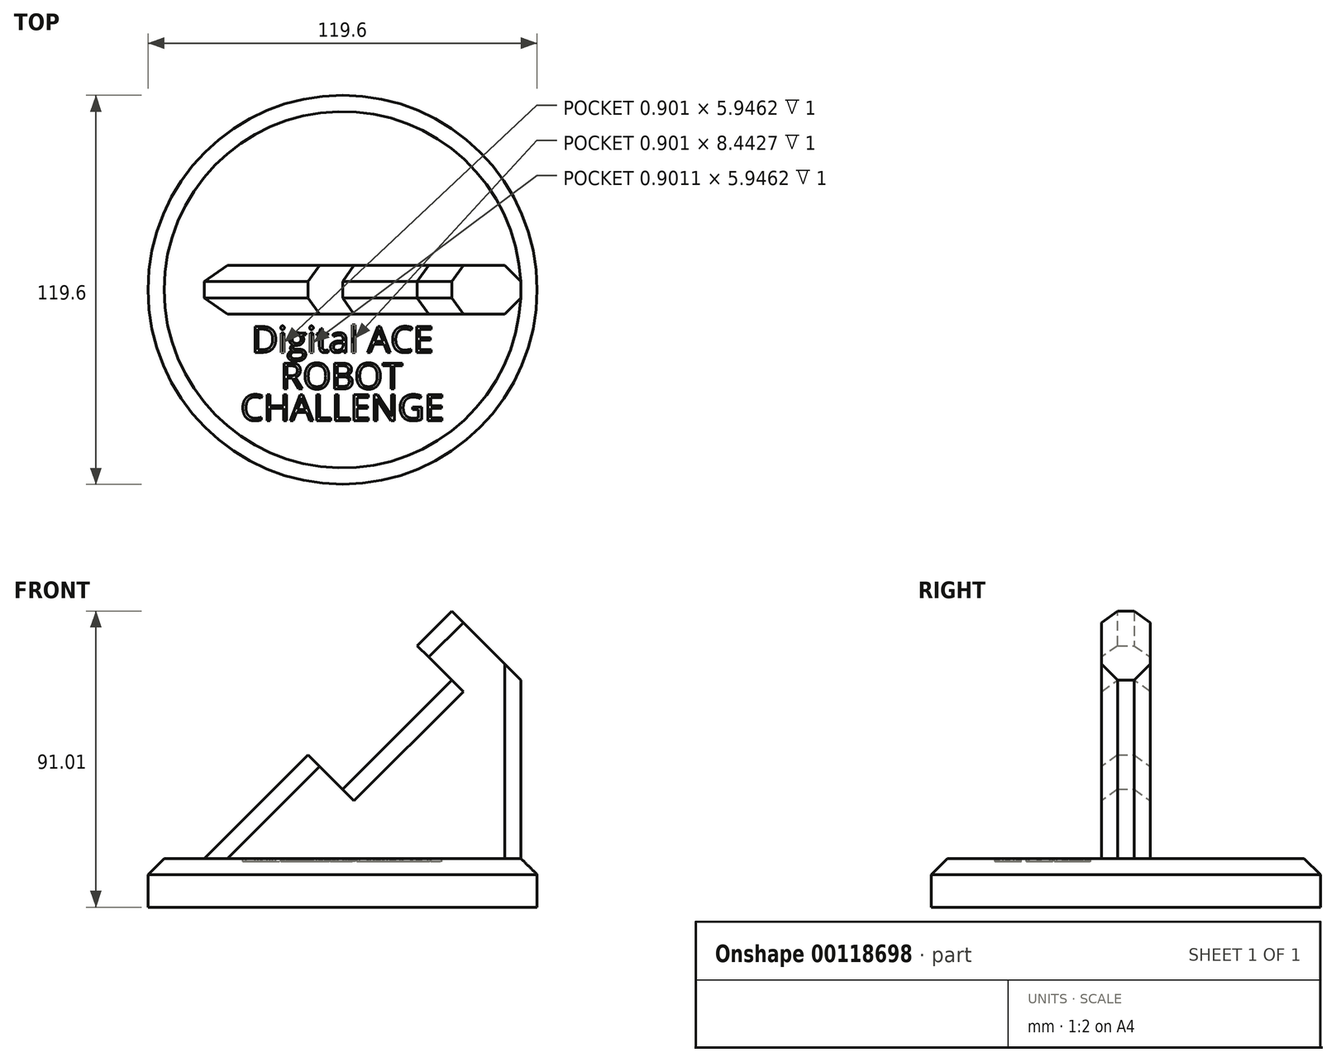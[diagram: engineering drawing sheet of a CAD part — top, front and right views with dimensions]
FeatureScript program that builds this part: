
annotation { "Feature Type Name" : "Feature", "Feature Type Description" : "" }
export const myFeature = defineFeature(function(context is Context, id is Id, definition is map)
    precondition{}
    {
        {
            var Q0;
            Q0=qCreatedBy(makeId("Front.planeOp"),FACE);
            var sketch = newSketch(context, id + "F0", { "sketchPlane" : qUnion([Q0])});
            skLineSegment(sketch, "E0", {"start": v(-80, 0) * mm, "end": v(0, 80) * mm, "construction": true});
            skLineSegment(sketch, "E1", {"start": v(-80, 0) * mm, "end": v(-46.41, 33.59) * mm});
            skLineSegment(sketch, "E2", {"start": v(-46.41, 33.59) * mm, "end": v(-57.02, 44.2) * mm});
            skLineSegment(sketch, "E3", {"start": v(-80, 0) * mm, "end": v(-90.6, 10.6) * mm});
            skLineSegment(sketch, "E4", {"start": v(-90.6, 10.6) * mm, "end": v(-101.21, 0) * mm});
            skLineSegment(sketch, "E5", {"start": v(-101.21, 0) * mm, "end": v(-80, -21.21) * mm});
            skLineSegment(sketch, "E6", {"start": v(-57.02, 44.2) * mm, "end": v(-46.41, 54.8) * mm});
            skLineSegment(sketch, "E7", {"start": v(-46.41, 54.8) * mm, "end": v(-25.2, 33.59) * mm});
            skLineSegment(sketch, "E8", {"start": v(-25.2, 33.59) * mm, "end": v(-25.2, -21.21) * mm});
            skLineSegment(sketch, "E9", {"start": v(-25.2, -21.21) * mm, "end": v(-80, -21.21) * mm, "construction": true});
            skLineSegment(sketch, "E10", {"start": v(-52.6, -21.21) * mm, "end": v(-52.6, 73.71) * mm, "construction": true});
            skLineSegment(sketch, "E11", {"start": v(-52.6, -21.21) * mm, "end": v(-52.6, -70.46) * mm, "construction": true});
            skLineSegment(sketch, "E12", {"start": v(-80, -21.21) * mm, "end": v(-80, -75.81) * mm, "construction": true});
            skLineSegment(sketch, "E13.MirrorCS", {"start": v(-134.8, -21.21) * mm, "end": v(-80, -21.21) * mm, "construction": true});
            skLineSegment(sketch, "E14", {"start": v(-80, -21.21) * mm, "end": v(-134.8, -21.21) * mm});
            skLineSegment(sketch, "E15", {"start": v(-134.8, -21.21) * mm, "end": v(-139.8, -21.21) * mm});
            skLineSegment(sketch, "E16", {"start": v(-139.8, -21.21) * mm, "end": v(-139.8, -36.21) * mm});
            skLineSegment(sketch, "E17", {"start": v(-139.8, -36.21) * mm, "end": v(-80, -36.21) * mm});
            skLineSegment(sketch, "E18", {"start": v(-80, -21.21) * mm, "end": v(-80, -36.21) * mm});
            skLineSegment(sketch, "E19", {"start": v(-80, -21.21) * mm, "end": v(-25.2, -21.21) * mm});
            skLineSegment(sketch, "E20.MirrorCS", {"start": v(-25.2, -21.21) * mm, "end": v(-20.2, -21.21) * mm, "construction": true});
            skLineSegment(sketch, "E21.MirrorCS", {"start": v(-20.2, -21.21) * mm, "end": v(-20.2, -36.21) * mm, "construction": true});
            skLineSegment(sketch, "E22.MirrorCS", {"start": v(-20.2, -36.21) * mm, "end": v(-80, -36.21) * mm, "construction": true});
            skSolve(sketch);
        }
        {
            var Q0;
            Q0=makeQuery(id+"F0.imprint","IMPRINT",FACE,{"disambiguationData":[TD([[makeQuery(id+"F0.imprint","IMPRINT",EDGE,{"derivedFrom":sQuery(id+"F0.wireOp",EDGE,"E1")}),-1.0]])]});
            extrude(context, id + "F1", {"entities" : qUnion([Q0]), "depth" : 15 * mm, "symmetric" : true});
        }
        {
            var Q0;
            Q0=makeQuery(id+"F0.imprint","IMPRINT",FACE,{"disambiguationData":[TD([[makeQuery(id+"F0.imprint","IMPRINT",EDGE,{"derivedFrom":sQuery(id+"F0.wireOp",EDGE,"E14")}),1.0]])]});
            var Q1;
            Q1=sQuery(id+"F0.wireOp",EDGE,"E18");
            revolve(context, id + "F2", {"operationType" : NewBodyOperationType.ADD, "entities" : qUnion([Q0]), "axis" : qUnion([Q1]), "revolveType" : RevolveType.FULL});
        }
        {
            var Q0;
            Q0=makeQuery(id+"F2.opRevolve","SWEPT_EDGE",EDGE,{"disambiguationData":[OSD([sQuery(id+"F0.wireOp",EDGE,"E15"),sQuery(id+"F0.wireOp",EDGE,"E16")])]});
            chamfer(context, id + "F3", {"entities" : qUnion([Q0]), "width" : 5 * mm, "tangentPropagation" : true});
        }
        {
            var Q0;
            Q0=makeQuery(id+"F1.opExtrude","CAP_EDGE",EDGE,{"disambiguationData":[OSD([sQuery(id+"F0.wireOp",EDGE,"E8")])],"isStart":false});
            var Q1;
            Q1=makeQuery(id+"F1.opExtrude","CAP_EDGE",EDGE,{"disambiguationData":[OSD([sQuery(id+"F0.wireOp",EDGE,"E8")])],"isStart":true});
            var Q2;
            Q2=makeQuery(id+"F1.opExtrude","CAP_EDGE",EDGE,{"disambiguationData":[OSD([sQuery(id+"F0.wireOp",EDGE,"E1")])],"isStart":false});
            var Q3;
            Q3=makeQuery(id+"F1.opExtrude","CAP_EDGE",EDGE,{"disambiguationData":[OSD([sQuery(id+"F0.wireOp",EDGE,"E1")])],"isStart":true});
            chamfer(context, id + "F4", {"entities" : qUnion([Q0, Q1, Q2, Q3]), "width" : 5 * mm, "tangentPropagation" : true});
        }
        {
            var Q0;
            Q0=makeQuery(id+"F1.opExtrude","SWEPT_FACE",FACE,{"disambiguationData":[OSD([sQuery(id+"F0.wireOp",EDGE,"E7")])]});
            var sketch = newSketch(context, id + "F5", { "sketchPlane" : qUnion([Q0])});
            skLineSegment(sketch, "E23", {"start": v(-71.57, -7.5) * mm, "end": v(-56.57, -7.5) * mm, "construction": true});
            skCircle(sketch, "E24", {"center": v(-64.07, 0) * mm, "radius": 4.25 * mm});
            skPoint(sketch, "E24.centerSnap0", {"position": v(-64.07, -7.5) * mm});
            skPoint(sketch, "E24.centerSnap1", {"position": v(-71.57, 0) * mm});
            skSolve(sketch);
        }
        {
            var Q0;
            Q0 = qSketchRegion(id + "F5", true);
            var Q1;
            Q1=makeQuery(id+"F1.opExtrude","SWEPT_FACE",FACE,{"disambiguationData":[OSD([sQuery(id+"F0.wireOp",EDGE,"E5")])]});
            extrude(context, id + "F6", {"entities" : qUnion([Q0]), "operationType" : NewBodyOperationType.REMOVE, "endBound" : BoundingType.UP_TO_SURFACE, "oppositeDirection" : true, "endBoundEntityFace" : qUnion([Q1]), "depth" : 25 * mm});
        }
        {
            var Q0;
            Q0=makeQuery(id+"F1.opExtrude","CAP_EDGE",EDGE,{"disambiguationData":[OSD([sQuery(id+"F0.wireOp",EDGE,"E6")])],"isStart":false});
            var Q1;
            Q1=makeQuery(id+"F1.opExtrude","CAP_EDGE",EDGE,{"disambiguationData":[OSD([sQuery(id+"F0.wireOp",EDGE,"E6")])],"isStart":true});
            var Q2;
            Q2=makeQuery(id+"F1.opExtrude","CAP_EDGE",EDGE,{"disambiguationData":[OSD([sQuery(id+"F0.wireOp",EDGE,"E4")])],"isStart":true});
            var Q3;
            Q3=makeQuery(id+"F1.opExtrude","CAP_EDGE",EDGE,{"disambiguationData":[OSD([sQuery(id+"F0.wireOp",EDGE,"E4")])],"isStart":false});
            chamfer(context, id + "F7", {"entities" : qUnion([Q0, Q1, Q2, Q3]), "width" : 5 * mm, "tangentPropagation" : true});
        }
        {
            var Q0;
            Q0=makeQuery(id+"F1.opExtrude","SWEPT_FACE",FACE,{"disambiguationData":[OSD([sQuery(id+"F0.wireOp",EDGE,"E5")])]});
            var Q1;
            Q1=makeQuery(id+"F2.opRevolve","SWEPT_FACE",FACE,{"disambiguationData":[OSD([sQuery(id+"F0.wireOp",EDGE,"E14"),sQuery(id+"F0.wireOp",EDGE,"E15")])]});
            extrude(context, id + "F8", {"entities" : qUnion([Q0]), "operationType" : NewBodyOperationType.ADD, "endBound" : BoundingType.UP_TO_SURFACE, "endBoundEntityFace" : qUnion([Q1]), "depth" : 25 * mm});
        }
        {
            var Q0;
            {var subQ0=sQuery(id+"F0.wireOp",EDGE,"E4");var subQ12=sQuery(id+"F0.wireOp",EDGE,"E15");Q0=makeQuery(id+"F8.boolean.opBoolean","SPLIT",FACE,{"disambiguationData":[TD([makeQuery(id+"F1.opExtrude","SWEPT_FACE",FACE,{"disambiguationData":[OSD([subQ0])]})])],"derivedFrom":makeQuery(id+"F2.opRevolve","SWEPT_FACE",FACE,{"disambiguationData":[OSD([sQuery(id+"F0.wireOp",EDGE,"E14"),subQ12])]})});}
            var sketch = newSketch(context, id + "F9", { "sketchPlane" : qUnion([Q0])});
            skText(sketch, "E25", { "text": "Digital ACE", "fontName": "OpenSans-Regular.ttf"});
            skText(sketch, "E26", { "text": "ROBOT", "fontName": "OpenSans-Regular.ttf"});
            skText(sketch, "E27", { "text": "CHALLENGE", "fontName": "OpenSans-Regular.ttf"});
            skLineSegment(sketch, "E28", {"start": v(-80, -22.5) * mm, "end": v(-80, 0) * mm, "construction": true});
            skLineSegment(sketch, "E29", {"start": v(-80, 0) * mm, "end": v(-80, -86.9) * mm, "construction": true});
            skLineSegment(sketch, "E30", {"start": v(-80, 0) * mm, "end": v(-80, 90.1) * mm, "construction": true});
            const initialGuessF9  = {"E25": [-0.10794, -0.01925, 1, 0, 0.008], "E26": [-0.09907, -0.0305, 1, 0, 0.008], "E27": [-0.11133, -0.0402, 1, 0, 0.008]};
            skSetInitialGuess(sketch, initialGuessF9);
            skSolve(sketch);
        }
        {
            var Q0;
            Q0 = qSketchRegion(id + "F9", true);
            extrude(context, id + "F10", {"entities" : qUnion([Q0]), "operationType" : NewBodyOperationType.REMOVE, "oppositeDirection" : true, "depth" : 1 * mm});
        }
    });
